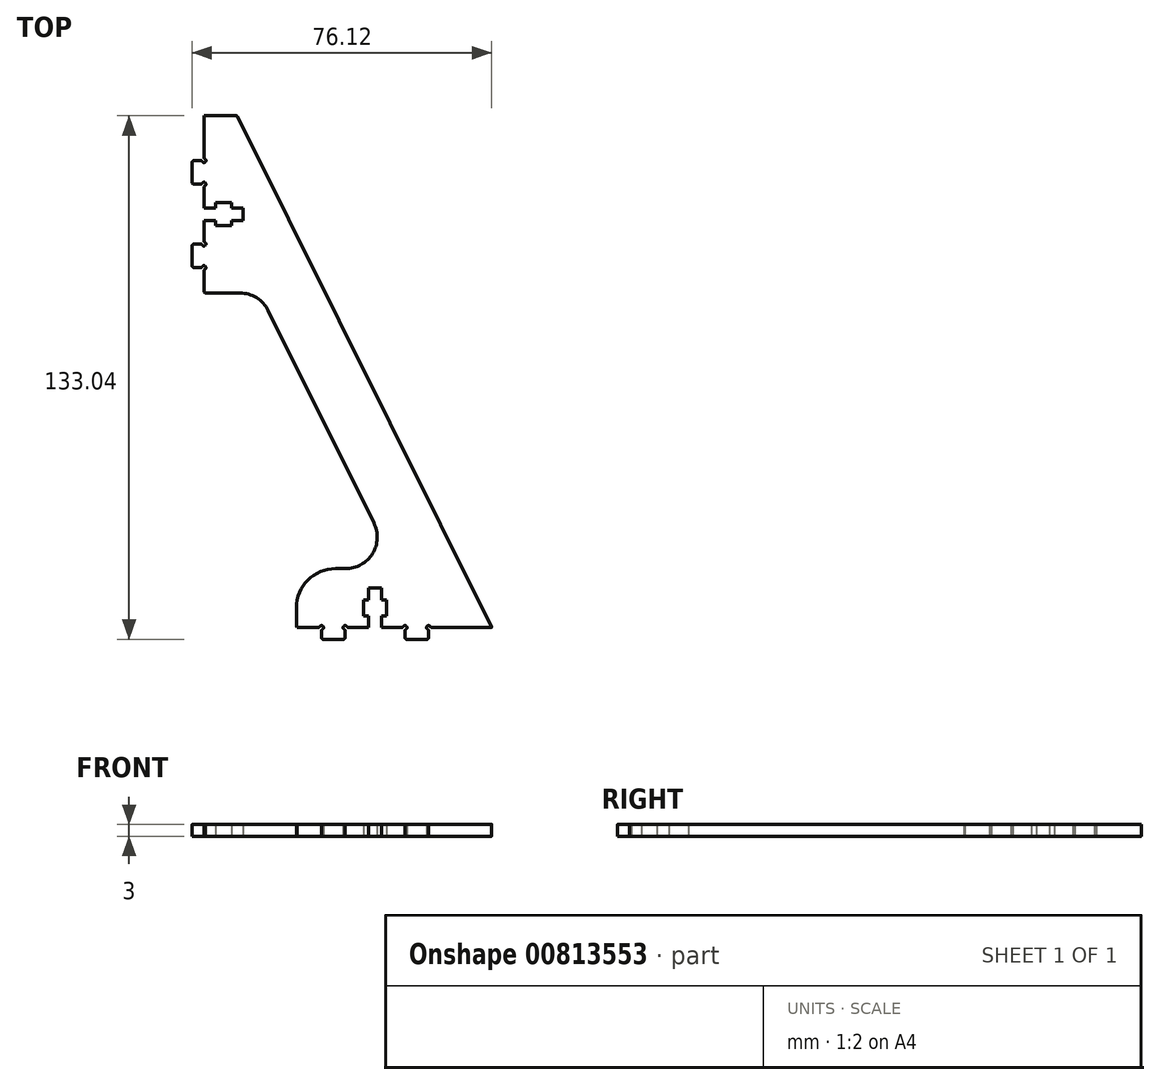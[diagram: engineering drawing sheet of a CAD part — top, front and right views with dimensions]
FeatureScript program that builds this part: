
annotation { "Feature Type Name" : "Feature", "Feature Type Description" : "" }
export const myFeature = defineFeature(function(context is Context, id is Id, definition is map)
    precondition{}
    {
        {
            var Q0;
            Q0=qCreatedBy(makeId("Top.planeOp"),FACE);
            var sketch = newSketch(context, id + "F0", { "sketchPlane" : qUnion([Q0])});
            skArc(sketch, "E0", {"start": v(-6.05, -63.52) * mm, "mid": v(-5.8, -63.45) * mm, "end": v(-5.61, -63.27) * mm});
            skArc(sketch, "E1", {"start": v(-4.93, -63.95) * mm, "mid": v(-4.83, -63.17) * mm, "end": v(-5.61, -63.27) * mm});
            skArc(sketch, "E2", {"start": v(-4.93, -63.95) * mm, "mid": v(-5.11, -64.14) * mm, "end": v(-5.18, -64.39) * mm});
            skLineSegment(sketch, "E3", {"start": v(-5.18, -64.39) * mm, "end": v(-5.18, -66.02) * mm});
            skArc(sketch, "E4", {"start": v(-5.18, -66.02) * mm, "mid": v(-5.04, -66.38) * mm, "end": v(-4.68, -66.52) * mm});
            skLineSegment(sketch, "E5", {"start": v(-4.68, -66.52) * mm, "end": v(0.32, -66.52) * mm});
            skArc(sketch, "E6", {"start": v(0.32, -66.52) * mm, "mid": v(0.67, -66.38) * mm, "end": v(0.82, -66.02) * mm});
            skLineSegment(sketch, "E7", {"start": v(0.82, -66.02) * mm, "end": v(0.82, -64.39) * mm});
            skArc(sketch, "E8", {"start": v(0.82, -64.39) * mm, "mid": v(0.75, -64.14) * mm, "end": v(0.57, -63.95) * mm});
            skArc(sketch, "E9", {"start": v(1.25, -63.27) * mm, "mid": v(0.46, -63.17) * mm, "end": v(0.57, -63.95) * mm});
            skArc(sketch, "E10", {"start": v(1.25, -63.27) * mm, "mid": v(1.43, -63.45) * mm, "end": v(1.68, -63.52) * mm});
            skLineSegment(sketch, "E11", {"start": v(1.68, -63.52) * mm, "end": v(6.82, -63.52) * mm});
            skLineSegment(sketch, "E12", {"start": v(6.82, -63.52) * mm, "end": v(6.82, -60.52) * mm});
            skLineSegment(sketch, "E13", {"start": v(6.82, -60.52) * mm, "end": v(5.54, -60.52) * mm});
            skLineSegment(sketch, "E14", {"start": v(5.54, -60.52) * mm, "end": v(5.54, -56.52) * mm});
            skLineSegment(sketch, "E15", {"start": v(5.54, -56.52) * mm, "end": v(6.82, -56.52) * mm});
            skLineSegment(sketch, "E16", {"start": v(6.82, -56.52) * mm, "end": v(6.82, -53.52) * mm});
            skLineSegment(sketch, "E17", {"start": v(6.82, -53.52) * mm, "end": v(10.02, -53.52) * mm});
            skLineSegment(sketch, "E18", {"start": v(10.02, -53.52) * mm, "end": v(10.02, -56.52) * mm});
            skLineSegment(sketch, "E19", {"start": v(10.02, -56.52) * mm, "end": v(11.3, -56.52) * mm});
            skLineSegment(sketch, "E20", {"start": v(11.3, -56.52) * mm, "end": v(11.3, -60.52) * mm});
            skLineSegment(sketch, "E21", {"start": v(11.3, -60.52) * mm, "end": v(10.02, -60.52) * mm});
            skLineSegment(sketch, "E22", {"start": v(10.02, -60.52) * mm, "end": v(10.02, -63.52) * mm});
            skLineSegment(sketch, "E23", {"start": v(10.02, -63.52) * mm, "end": v(15.15, -63.52) * mm});
            skArc(sketch, "E24", {"start": v(15.15, -63.52) * mm, "mid": v(15.4, -63.45) * mm, "end": v(15.59, -63.27) * mm});
            skArc(sketch, "E25", {"start": v(16.27, -63.95) * mm, "mid": v(16.37, -63.17) * mm, "end": v(15.59, -63.27) * mm});
            skArc(sketch, "E26", {"start": v(16.27, -63.95) * mm, "mid": v(16.09, -64.14) * mm, "end": v(16.02, -64.39) * mm});
            skLineSegment(sketch, "E27", {"start": v(16.02, -64.39) * mm, "end": v(16.02, -66.02) * mm});
            skArc(sketch, "E28", {"start": v(16.02, -66.02) * mm, "mid": v(16.16, -66.38) * mm, "end": v(16.52, -66.52) * mm});
            skLineSegment(sketch, "E29", {"start": v(16.52, -66.52) * mm, "end": v(21.52, -66.52) * mm});
            skArc(sketch, "E30", {"start": v(21.52, -66.52) * mm, "mid": v(21.87, -66.38) * mm, "end": v(22.02, -66.02) * mm});
            skLineSegment(sketch, "E31", {"start": v(22.02, -66.02) * mm, "end": v(22.02, -64.39) * mm});
            skArc(sketch, "E32", {"start": v(22.02, -64.39) * mm, "mid": v(21.95, -64.14) * mm, "end": v(21.77, -63.95) * mm});
            skArc(sketch, "E33", {"start": v(22.45, -63.27) * mm, "mid": v(21.66, -63.17) * mm, "end": v(21.77, -63.95) * mm});
            skArc(sketch, "E34", {"start": v(22.45, -63.27) * mm, "mid": v(22.63, -63.45) * mm, "end": v(22.88, -63.52) * mm});
            skArc(sketch, "E35", {"start": v(-35.06, 55.99) * mm, "mid": v(-35, 55.74) * mm, "end": v(-34.8, 55.56) * mm});
            skArc(sketch, "E36", {"start": v(-35.5, 54.87) * mm, "mid": v(-34.7, 54.77) * mm, "end": v(-34.8, 55.56) * mm});
            skArc(sketch, "E37", {"start": v(-35.5, 54.87) * mm, "mid": v(-35.67, 55.06) * mm, "end": v(-35.92, 55.12) * mm});
            skLineSegment(sketch, "E38", {"start": v(-35.92, 55.12) * mm, "end": v(-37.56, 55.12) * mm});
            skLineSegment(sketch, "E39", {"start": v(-37.56, 49.12) * mm, "end": v(-35.92, 49.12) * mm});
            skArc(sketch, "E40", {"start": v(-35.92, 49.12) * mm, "mid": v(-35.67, 49.19) * mm, "end": v(-35.5, 49.37) * mm});
            skArc(sketch, "E41", {"start": v(-34.8, 48.69) * mm, "mid": v(-34.7, 49.48) * mm, "end": v(-35.5, 49.37) * mm});
            skArc(sketch, "E42", {"start": v(-34.8, 48.69) * mm, "mid": v(-35, 48.5) * mm, "end": v(-35.06, 48.26) * mm});
            skLineSegment(sketch, "E43", {"start": v(-35.06, 48.26) * mm, "end": v(-35.06, 43.12) * mm});
            skLineSegment(sketch, "E44", {"start": v(-35.06, 43.12) * mm, "end": v(-32.06, 43.12) * mm});
            skLineSegment(sketch, "E45", {"start": v(-32.06, 43.12) * mm, "end": v(-32.06, 44.4) * mm});
            skLineSegment(sketch, "E46", {"start": v(-32.06, 44.4) * mm, "end": v(-28.06, 44.4) * mm});
            skLineSegment(sketch, "E47", {"start": v(-28.06, 44.4) * mm, "end": v(-28.06, 43.12) * mm});
            skLineSegment(sketch, "E48", {"start": v(-28.06, 43.12) * mm, "end": v(-25.06, 43.12) * mm});
            skLineSegment(sketch, "E49", {"start": v(-25.06, 43.12) * mm, "end": v(-25.06, 39.92) * mm});
            skLineSegment(sketch, "E50", {"start": v(-25.06, 39.92) * mm, "end": v(-28.06, 39.92) * mm});
            skLineSegment(sketch, "E51", {"start": v(-28.06, 39.92) * mm, "end": v(-28.06, 38.65) * mm});
            skLineSegment(sketch, "E52", {"start": v(-28.06, 38.65) * mm, "end": v(-32.06, 38.65) * mm});
            skLineSegment(sketch, "E53", {"start": v(-32.06, 38.65) * mm, "end": v(-32.06, 39.92) * mm});
            skLineSegment(sketch, "E54", {"start": v(-32.06, 39.92) * mm, "end": v(-35.06, 39.92) * mm});
            skLineSegment(sketch, "E55", {"start": v(-35.06, 39.92) * mm, "end": v(-35.06, 34.79) * mm});
            skArc(sketch, "E56", {"start": v(-35.06, 34.79) * mm, "mid": v(-35, 34.54) * mm, "end": v(-34.8, 34.36) * mm});
            skArc(sketch, "E57", {"start": v(-35.5, 33.67) * mm, "mid": v(-34.7, 33.57) * mm, "end": v(-34.8, 34.36) * mm});
            skArc(sketch, "E58", {"start": v(-35.5, 33.67) * mm, "mid": v(-35.67, 33.86) * mm, "end": v(-35.92, 33.92) * mm});
            skLineSegment(sketch, "E59", {"start": v(-35.92, 33.92) * mm, "end": v(-37.56, 33.92) * mm});
            skLineSegment(sketch, "E60", {"start": v(-37.56, 27.92) * mm, "end": v(-35.92, 27.92) * mm});
            skArc(sketch, "E61", {"start": v(-35.92, 27.92) * mm, "mid": v(-35.67, 27.99) * mm, "end": v(-35.5, 28.17) * mm});
            skArc(sketch, "E62", {"start": v(-34.8, 27.49) * mm, "mid": v(-34.7, 28.28) * mm, "end": v(-35.5, 28.17) * mm});
            skArc(sketch, "E63", {"start": v(-34.8, 27.49) * mm, "mid": v(-35, 27.3) * mm, "end": v(-35.06, 27.06) * mm});
            skArc(sketch, "E64", {"start": v(-37.56, 55.12) * mm, "mid": v(-37.91, 54.98) * mm, "end": v(-38.06, 54.62) * mm});
            skLineSegment(sketch, "E65", {"start": v(-38.06, 54.62) * mm, "end": v(-38.06, 49.62) * mm});
            skArc(sketch, "E66", {"start": v(-38.06, 49.62) * mm, "mid": v(-37.91, 49.27) * mm, "end": v(-37.56, 49.12) * mm});
            skArc(sketch, "E67", {"start": v(-37.56, 33.92) * mm, "mid": v(-37.91, 33.78) * mm, "end": v(-38.06, 33.42) * mm});
            skLineSegment(sketch, "E68", {"start": v(-38.06, 33.42) * mm, "end": v(-38.06, 28.42) * mm});
            skArc(sketch, "E69", {"start": v(-38.06, 28.42) * mm, "mid": v(-37.91, 28.07) * mm, "end": v(-37.56, 27.92) * mm});
            skLineSegment(sketch, "E70", {"start": v(-35.06, 66.52) * mm, "end": v(-35.06, 55.99) * mm});
            skArc(sketch, "E71", {"start": v(-1.58, -48.52) * mm, "mid": v(-8.65, -51.45) * mm, "end": v(-11.58, -58.52) * mm});
            skLineSegment(sketch, "E72", {"start": v(-35.06, 66.52) * mm, "end": v(-26.91, 66.52) * mm});
            skArc(sketch, "E73", {"start": v(-26.47, 66.25) * mm, "mid": v(-26.65, 66.45) * mm, "end": v(-26.91, 66.52) * mm});
            skLineSegment(sketch, "E74", {"start": v(22.88, -63.52) * mm, "end": v(37.96, -63.52) * mm});
            skLineSegment(sketch, "E75", {"start": v(-26.47, 66.25) * mm, "end": v(38.05, -63.38) * mm});
            skArc(sketch, "E76", {"start": v(37.96, -63.52) * mm, "mid": v(38.04, -63.47) * mm, "end": v(38.05, -63.38) * mm});
            skLineSegment(sketch, "E77", {"start": v(-1.58, -48.52) * mm, "end": v(0.98, -48.52) * mm});
            skArc(sketch, "E78", {"start": v(0.98, -48.52) * mm, "mid": v(7.78, -44.73) * mm, "end": v(8.14, -36.96) * mm});
            skLineSegment(sketch, "E79", {"start": v(-18.73, 17.04) * mm, "end": v(8.14, -36.96) * mm});
            skArc(sketch, "E80", {"start": v(-18.73, 17.04) * mm, "mid": v(-21.68, 20.28) * mm, "end": v(-25.9, 21.48) * mm});
            skLineSegment(sketch, "E81", {"start": v(-11.58, -63.27) * mm, "end": v(-11.58, -58.52) * mm});
            skLineSegment(sketch, "E82", {"start": v(-11.33, -63.52) * mm, "end": v(-6.05, -63.52) * mm});
            skLineSegment(sketch, "E83", {"start": v(-11.58, -63.27) * mm, "end": v(-11.33, -63.52) * mm});
            skLineSegment(sketch, "E84", {"start": v(-35.06, 27.06) * mm, "end": v(-35.06, 21.73) * mm});
            skLineSegment(sketch, "E85", {"start": v(-34.8, 21.48) * mm, "end": v(-25.9, 21.48) * mm});
            skLineSegment(sketch, "E86", {"start": v(-35.06, 21.73) * mm, "end": v(-34.8, 21.48) * mm});
            skSolve(sketch);
        }
        {
            var Q0;
            Q0=qSketchRegion(id+"F0",true);
            extrude(context, id + "F1", {"entities" : qUnion([Q0]), "depth" : 3 * mm, "offsetDistance" : 25 * mm});
        }
    });
